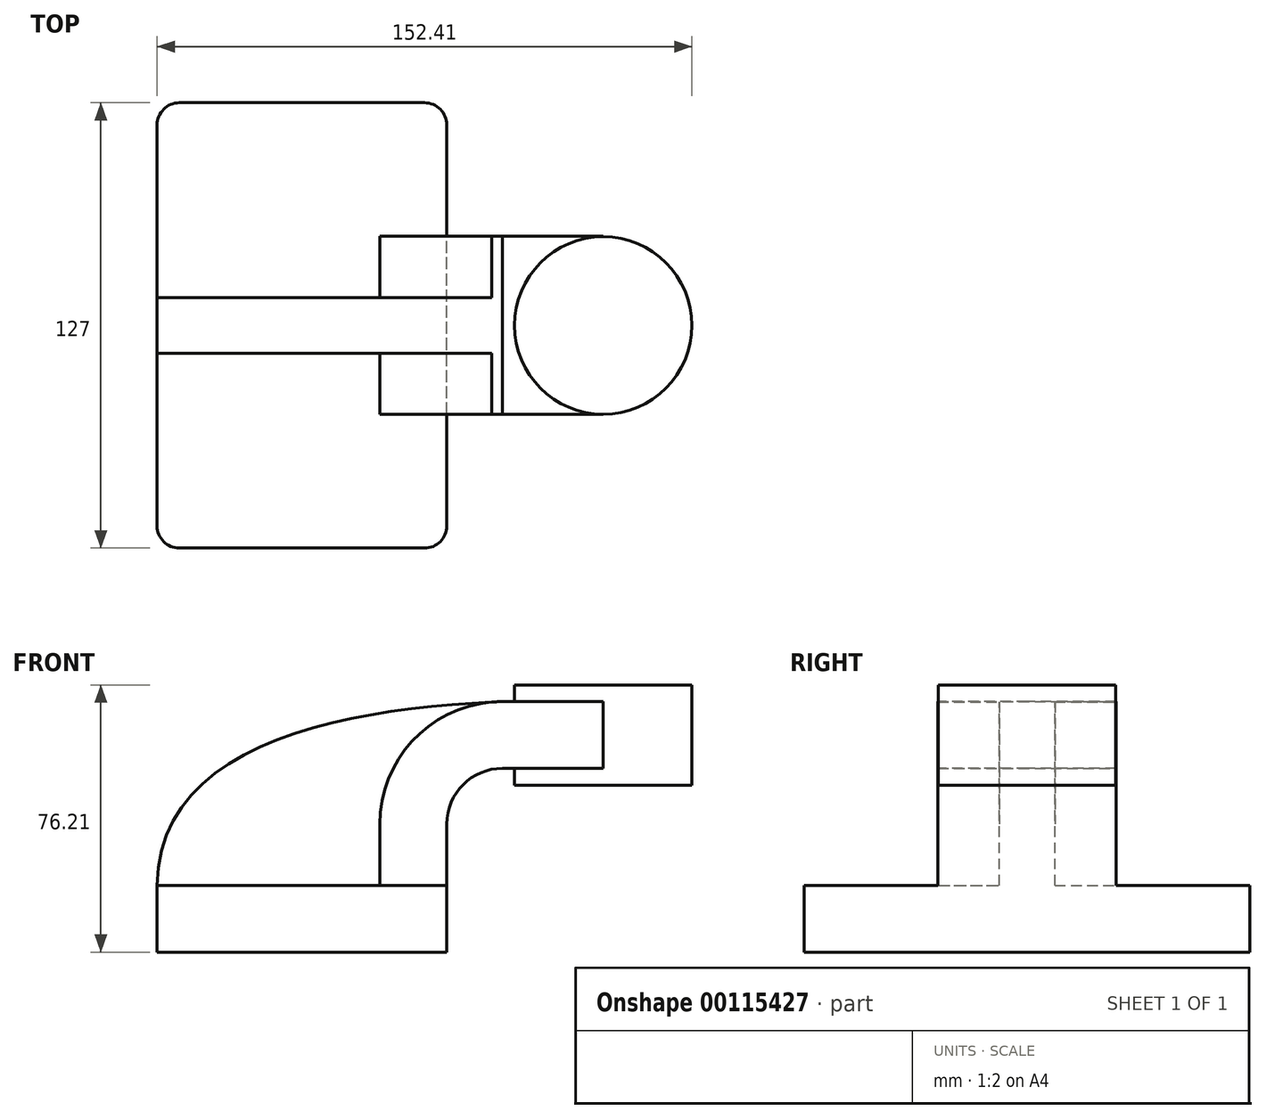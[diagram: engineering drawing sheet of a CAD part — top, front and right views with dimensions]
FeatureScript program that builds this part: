
annotation { "Feature Type Name" : "Feature", "Feature Type Description" : "" }
export const myFeature = defineFeature(function(context is Context, id is Id, definition is map)
    precondition{}
    {
        {
            var Q0;
            Q0=qCreatedBy(makeId("Front.planeOp"),FACE);
            var sketch = newSketch(context, id + "F0", { "sketchPlane" : qUnion([Q0])});
            skLineSegment(sketch, "E0.bottom", {"start": v(41.28, -9.52) * mm, "end": v(-41.28, -9.53) * mm});
            skLineSegment(sketch, "E0.top", {"start": v(41.28, 9.53) * mm, "end": v(-41.28, 9.52) * mm});
            skLineSegment(sketch, "E0.left", {"start": v(41.28, -9.52) * mm, "end": v(41.28, 9.53) * mm});
            skLineSegment(sketch, "E0.right", {"start": v(-41.28, -9.53) * mm, "end": v(-41.28, 9.52) * mm});
            skPoint(sketch, "E0.middle", {"position": v(0, 0) * mm});
            skLineSegment(sketch, "E1.bottom", {"start": v(111.12, 38.1) * mm, "end": v(60.33, 38.1) * mm});
            skLineSegment(sketch, "E1.top", {"start": v(111.12, 66.68) * mm, "end": v(60.33, 66.68) * mm});
            skLineSegment(sketch, "E1.left", {"start": v(111.12, 38.1) * mm, "end": v(111.12, 66.68) * mm});
            skLineSegment(sketch, "E1.right", {"start": v(60.33, 38.1) * mm, "end": v(60.33, 66.67) * mm});
            skPoint(sketch, "E1.middle", {"position": v(85.72, 52.39) * mm});
            skLineSegment(sketch, "E2", {"start": v(41.28, 9.53) * mm, "end": v(41.28, 12.71) * mm});
            skLineSegment(sketch, "E3", {"start": v(41.28, 12.71) * mm, "end": v(41.28, 27) * mm});
            skArc(sketch, "E4", {"start": v(41.28, 27) * mm, "mid": v(45.92, 38.23) * mm, "end": v(57.15, 42.88) * mm});
            skLineSegment(sketch, "E5", {"start": v(57.15, 42.88) * mm, "end": v(85.84, 42.88) * mm});
            skLineSegment(sketch, "E6.0", {"start": v(57.15, 61.93) * mm, "end": v(85.84, 61.93) * mm});
            skArc(sketch, "E6.1", {"start": v(22.23, 27) * mm, "mid": v(32.45, 51.7) * mm, "end": v(57.15, 61.93) * mm});
            skLineSegment(sketch, "E6.2", {"start": v(22.23, 12.71) * mm, "end": v(22.23, 27) * mm});
            skLineSegment(sketch, "E6.3", {"start": v(22.23, 9.53) * mm, "end": v(22.23, 12.71) * mm});
            skFitSpline(sketch, "E7", {"points": [v(-41.28, 9.52) * mm, v(57.15, 61.93) * mm], "startDerivative": vector(0.73, 123.56) * mm, "endDerivative": vector(130.42, 5.23) * mm});
            skLineSegment(sketch, "E8", {"start": v(85.84, 38.1) * mm, "end": v(85.84, 66.68) * mm});
            skSolve(sketch);
        }
        {
            var Q0;
            Q0=makeQuery(id+"F0.imprint","IMPRINT",FACE,{"disambiguationData":[TD([[makeQuery(id+"F0.imprint","IMPRINT",EDGE,{"derivedFrom":sQuery(id+"F0.wireOp",EDGE,"E0.bottom")}),-1.0]])]});
            extrude(context, id + "F1", {"entities" : qUnion([Q0]), "endBound" : BoundingType.SYMMETRIC, "depth" : 127 * mm});
        }
        {
            var Q0;
            {var subQ8=sQuery(id+"F0.wireOp",EDGE,"E2");Q0=makeQuery(id+"F0.imprint","IMPRINT",FACE,{"disambiguationData":[TD([[makeQuery(id+"F0.imprint","IMPRINT",EDGE,{"derivedFrom":subQ8}),1.0]])]});}
            var Q1;
            {var subQ0=sQuery(id+"F0.wireOp",EDGE,"E5");var subQ1=sQuery(id+"F0.wireOp",EDGE,"E1.right");var subQ2=makeQuery(id+"F0.imprint","INTERSECT",VERTEX,{"derivedFrom":[subQ1,subQ0]});Q1=makeQuery(id+"F0.imprint","IMPRINT",FACE,{"disambiguationData":[TD([[makeQuery(id+"F0.imprint","IMPRINT",EDGE,{"disambiguationData":[TD([[subQ2,-1.0]])],"derivedFrom":subQ1}),-1.0]])]});}
            extrude(context, id + "F2", {"entities" : qUnion([Q0, Q1]), "operationType" : NewBodyOperationType.ADD, "endBound" : BoundingType.SYMMETRIC, "depth" : 50.8 * mm});
        }
        {
            var Q0;
            {var subQ0=sQuery(id+"F0.wireOp",EDGE,"E6.2");Q0=makeQuery(id+"F0.imprint","IMPRINT",FACE,{"disambiguationData":[TD([[makeQuery(id+"F0.imprint","IMPRINT",EDGE,{"derivedFrom":subQ0}),1.0]])]});}
            extrude(context, id + "F3", {"entities" : qUnion([Q0]), "operationType" : NewBodyOperationType.ADD, "endBound" : BoundingType.SYMMETRIC, "depth" : 15.88 * mm});
        }
        {
            var Q0;
            {var subQ4=sQuery(id+"F0.wireOp",EDGE,"E1.left");Q0=makeQuery(id+"F0.imprint","IMPRINT",FACE,{"disambiguationData":[TD([[makeQuery(id+"F0.imprint","IMPRINT",EDGE,{"derivedFrom":subQ4}),1.0]])]});}
            var Q1;
            Q1=sQuery(id+"F0.wireOp",EDGE,"E8");
            revolve(context, id + "F4", {"operationType" : NewBodyOperationType.ADD, "entities" : qUnion([Q0]), "axis" : qUnion([Q1]), "revolveType" : RevolveType.FULL});
        }
        {
            var Q0;
            Q0=makeQuery(id+"F1.opExtrude","CAP_EDGE",EDGE,{"disambiguationData":[OSD([sQuery(id+"F0.wireOp",EDGE,"E0.left")])],"isStart":false});
            var Q1;
            Q1=makeQuery(id+"F1.opExtrude","CAP_EDGE",EDGE,{"disambiguationData":[OSD([sQuery(id+"F0.wireOp",EDGE,"E0.right")])],"isStart":false});
            var Q2;
            Q2=makeQuery(id+"F1.opExtrude","CAP_EDGE",EDGE,{"disambiguationData":[OSD([sQuery(id+"F0.wireOp",EDGE,"E0.right")])],"isStart":true});
            var Q3;
            Q3=makeQuery(id+"F1.opExtrude","CAP_EDGE",EDGE,{"disambiguationData":[OSD([sQuery(id+"F0.wireOp",EDGE,"E0.left")])],"isStart":true});
            fillet(context, id + "F5", {"entities" : qUnion([Q0, Q1, Q2, Q3]), "radius" : 6.35 * mm, "tangentPropagation" : true, "allowEdgeOverflow" : false});
        }
    });
